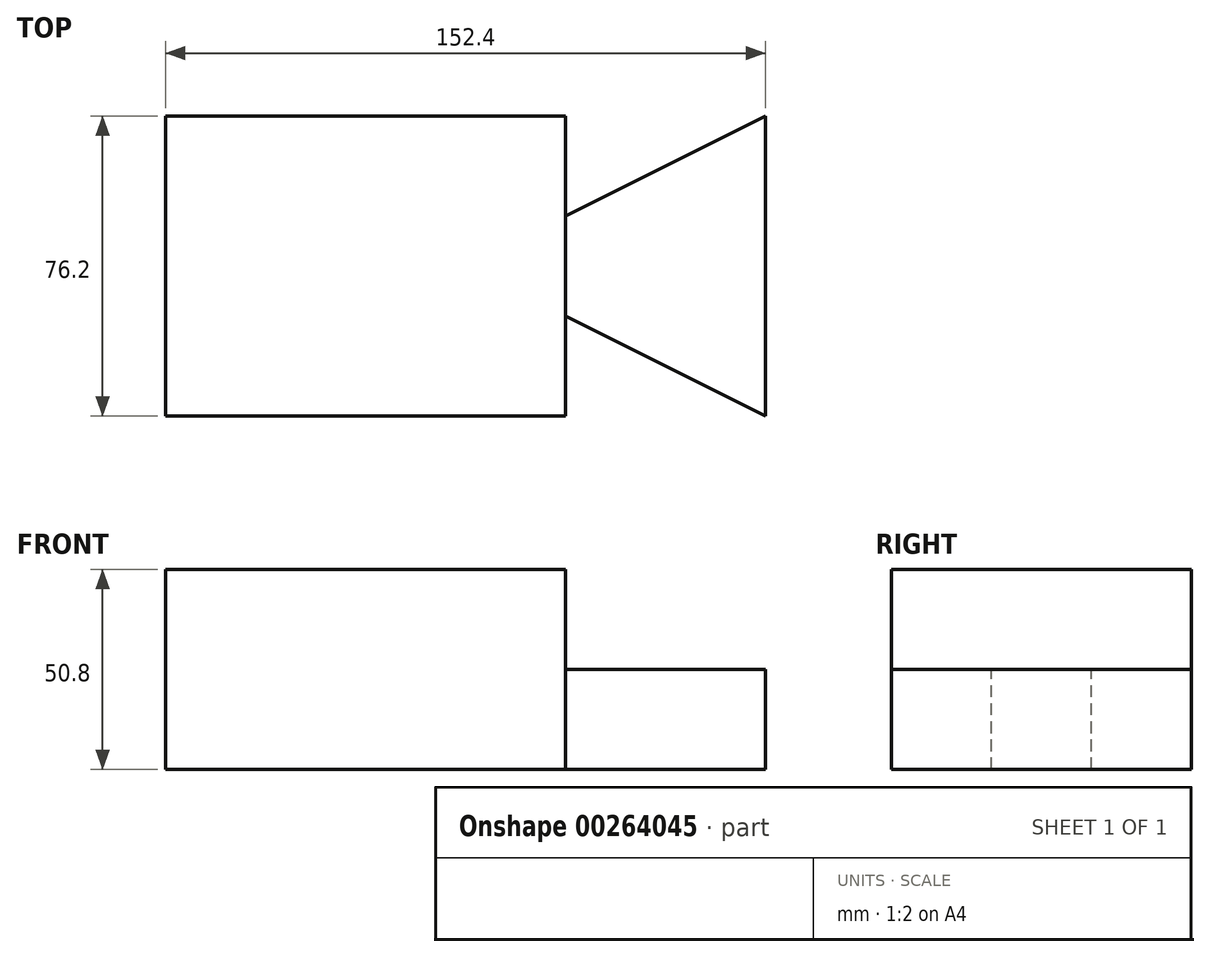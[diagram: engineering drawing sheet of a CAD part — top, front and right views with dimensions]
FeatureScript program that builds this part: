
annotation { "Feature Type Name" : "Feature", "Feature Type Description" : "" }
export const myFeature = defineFeature(function(context is Context, id is Id, definition is map)
    precondition{}
    {
        {
            var Q0;
            Q0=qCreatedBy(makeId("Front.planeOp"),FACE);
            var sketch = newSketch(context, id + "F0", { "sketchPlane" : qUnion([Q0])});
            skLineSegment(sketch, "E0.bottom", {"start": v(0, 0) * mm, "end": v(-101.6, 0) * mm});
            skLineSegment(sketch, "E0.top", {"start": v(0, 50.8) * mm, "end": v(-101.6, 50.8) * mm});
            skLineSegment(sketch, "E0.left", {"start": v(0, 0) * mm, "end": v(0, 50.8) * mm});
            skLineSegment(sketch, "E0.right", {"start": v(-101.6, 0) * mm, "end": v(-101.6, 50.8) * mm});
            skSolve(sketch);
        }
        {
            var Q0;
            Q0 = qSketchRegion(id + "F0", true);
            extrude(context, id + "F1", {"entities" : qUnion([Q0]), "depth" : 76.2 * mm});
        }
        {
            var Q0;
            Q0=makeQuery(id+"F1.opExtrude","SWEPT_FACE",FACE,{"disambiguationData":[OSD([sQuery(id+"F0.wireOp",EDGE,"E0.left")])]});
            var sketch = newSketch(context, id + "F2", { "sketchPlane" : qUnion([Q0])});
            skLineSegment(sketch, "E1.bottom", {"start": v(-76.2, 0) * mm, "end": v(-50.8, 0) * mm});
            skLineSegment(sketch, "E1.top", {"start": v(-76.2, 0) * mm, "end": v(-50.8, 0) * mm});
            skLineSegment(sketch, "E1.left", {"start": v(-76.2, 0) * mm, "end": v(-76.2, 0) * mm});
            skLineSegment(sketch, "E1.right", {"start": v(-50.8, 0) * mm, "end": v(-50.8, 0) * mm});
            skLineSegment(sketch, "E2.bottom", {"start": v(0, 0) * mm, "end": v(-25.4, 0) * mm});
            skLineSegment(sketch, "E2.top", {"start": v(0, 0) * mm, "end": v(-25.4, 0) * mm});
            skLineSegment(sketch, "E2.left", {"start": v(0, 0) * mm, "end": v(0, 0) * mm});
            skLineSegment(sketch, "E2.right", {"start": v(-25.4, 0) * mm, "end": v(-25.4, 0) * mm});
            skLineSegment(sketch, "E3", {"start": v(-25.4, 0) * mm, "end": v(-25.4, 25.4) * mm});
            skLineSegment(sketch, "E4", {"start": v(-50.8, 0) * mm, "end": v(-50.8, 25.4) * mm});
            skLineSegment(sketch, "E5", {"start": v(-50.8, 25.4) * mm, "end": v(-25.4, 25.4) * mm});
            skSolve(sketch);
        }
        {
            var Q0;
            Q0 = qSketchRegion(id + "F2", true);
            var Q1;
            {var subQ0=sQuery(id+"F2.wireOp",EDGE,"E3");Q1=makeQuery(id+"F2.imprint","IMPRINT",FACE,{"disambiguationData":[TD([[makeQuery(id+"F2.imprint","IMPRINT",EDGE,{"derivedFrom":subQ0}),1.0]])]});}
            extrude(context, id + "F3", {"entities" : qUnion([Q0, Q1]), "operationType" : NewBodyOperationType.ADD, "depth" : 50.8 * mm});
        }
        {
            var Q0;
            Q0=makeQuery(id+"F3.opExtrude","CAP_FACE",FACE,{"disambiguationData":[OSD([sQuery(id+"F0.wireOp",EDGE,"E0.bottom"),sQuery(id+"F0.wireOp",EDGE,"E0.left"),sQuery(id+"F2.wireOp",EDGE,"E3"),sQuery(id+"F2.wireOp",EDGE,"E4"),sQuery(id+"F2.wireOp",EDGE,"E5")])],"isStart":false});
            var sketch = newSketch(context, id + "F4", { "sketchPlane" : qUnion([Q0])});
            skLineSegment(sketch, "E6", {"start": v(-25.4, 0) * mm, "end": v(0, 0) * mm});
            skLineSegment(sketch, "E7", {"start": v(-50.8, 0) * mm, "end": v(-76.2, 0) * mm});
            skLineSegment(sketch, "E8", {"start": v(-76.2, 0) * mm, "end": v(-76.2, 25.4) * mm});
            skLineSegment(sketch, "E9", {"start": v(0, 0) * mm, "end": v(0, 25.4) * mm});
            skLineSegment(sketch, "E10", {"start": v(-76.2, 25.4) * mm, "end": v(0, 25.4) * mm});
            skSolve(sketch);
        }
        {
            var Q0;
            Q0=makeQuery(id+"F4.imprint","IMPRINT",FACE,{"disambiguationData":[TD([[makeQuery(id+"F4.imprint","IMPRINT",EDGE,{"derivedFrom":sQuery(id+"F4.wireOp",EDGE,"E7")}),-1.0]])]});
            var Q1;
            Q1=makeQuery(id+"F4.imprint","IMPRINT",FACE,{"disambiguationData":[TD([[makeQuery(id+"F4.imprint","IMPRINT",EDGE,{"derivedFrom":sQuery(id+"F4.wireOp",EDGE,"E6")}),1.0]])]});
            extrude(context, id + "F5", {"entities" : qUnion([Q0, Q1]), "operationType" : NewBodyOperationType.ADD, "oppositeDirection" : true, "depth" : 50.8 * mm});
        }
        {
            var Q0;
            {var subQ0=sQuery(id+"F4.wireOp",EDGE,"E10");Q0=makeQuery(id+"F5.boolean.opBoolean","MERGE",FACE,{"derivedFrom":[makeQuery(id+"F3.opExtrude","SWEPT_FACE",FACE,{"disambiguationData":[OSD([sQuery(id+"F2.wireOp",EDGE,"E5")])]}),makeQuery(id+"F5.opExtrude","SWEPT_FACE",FACE,{"disambiguationData":[OSD([subQ0]),TDD([makeQuery(id+"F4.imprint","IMPRINT",EDGE,{"disambiguationData":[TD([[makeQuery(id+"F4.imprint","INTERSECT",VERTEX,{"derivedFrom":[makeQuery(id+"F3.opExtrude","CAP_EDGE",EDGE,{"disambiguationData":[OSD([sQuery(id+"F2.wireOp",EDGE,"E4")])],"isStart":false}),subQ0]}),1.0]])],"derivedFrom":subQ0})])]}),makeQuery(id+"F5.opExtrude","SWEPT_FACE",FACE,{"disambiguationData":[OSD([subQ0]),TDD([makeQuery(id+"F4.imprint","IMPRINT",EDGE,{"disambiguationData":[TD([[makeQuery(id+"F4.imprint","INTERSECT",VERTEX,{"derivedFrom":[makeQuery(id+"F3.opExtrude","CAP_EDGE",EDGE,{"disambiguationData":[OSD([sQuery(id+"F2.wireOp",EDGE,"E3")])],"isStart":false}),subQ0]}),-1.0]])],"derivedFrom":subQ0})])]})]});}
            var sketch = newSketch(context, id + "F6", { "sketchPlane" : qUnion([Q0])});
            skLineSegment(sketch, "E11", {"start": v(0, -50.8) * mm, "end": v(50.8, -76.2) * mm});
            skLineSegment(sketch, "E12", {"start": v(0, -25.4) * mm, "end": v(50.8, 0) * mm});
            skLineSegment(sketch, "E13", {"start": v(0, -76.2) * mm, "end": v(0, -50.8) * mm});
            skLineSegment(sketch, "E14", {"start": v(0, -25.4) * mm, "end": v(0, 0) * mm});
            skSolve(sketch);
        }
        {
            var Q0;
            Q0=makeQuery(id+"F6.imprint","IMPRINT",FACE,{"disambiguationData":[TD([[makeQuery(id+"F6.imprint","IMPRINT",EDGE,{"derivedFrom":sQuery(id+"F6.wireOp",EDGE,"E12")}),1.0]])]});
            var Q1;
            Q1=makeQuery(id+"F6.imprint","IMPRINT",FACE,{"disambiguationData":[TD([[makeQuery(id+"F6.imprint","IMPRINT",EDGE,{"derivedFrom":sQuery(id+"F6.wireOp",EDGE,"E11")}),-1.0]])]});
            extrude(context, id + "F7", {"entities" : qUnion([Q0, Q1]), "operationType" : NewBodyOperationType.REMOVE, "oppositeDirection" : true, "depth" : 25.4 * mm});
        }
    });
